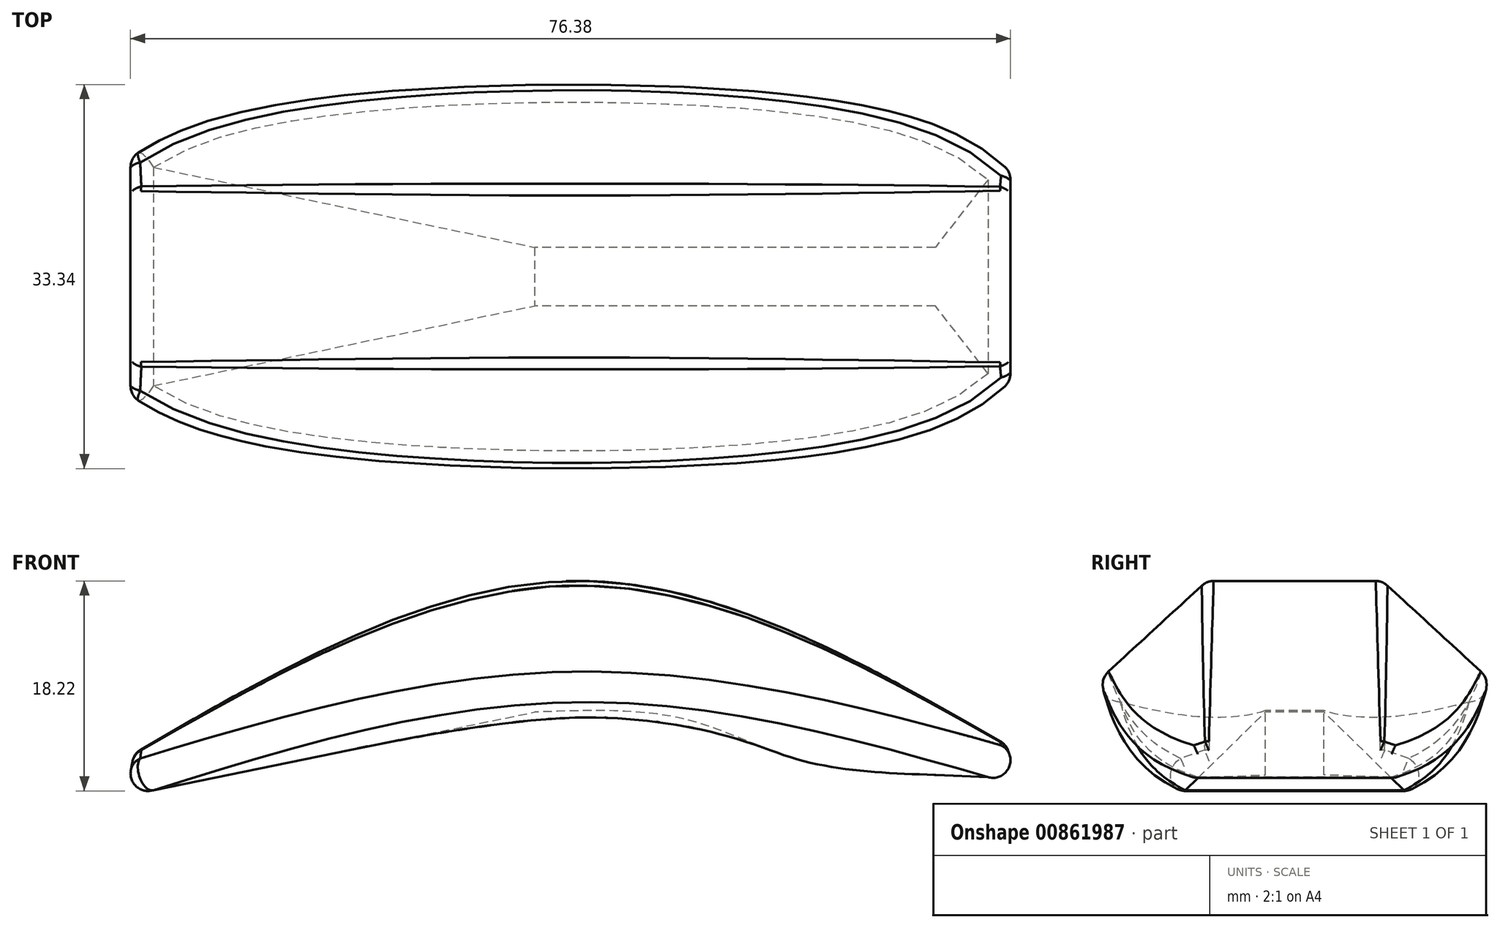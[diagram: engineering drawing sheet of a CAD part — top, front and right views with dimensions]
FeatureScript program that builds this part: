
annotation { "Feature Type Name" : "Feature", "Feature Type Description" : "" }
export const myFeature = defineFeature(function(context is Context, id is Id, definition is map)
    precondition{}
    {
        {
            var Q0;
            Q0=qCreatedBy(makeId("Front.planeOp"),FACE);
            var sketch = newSketch(context, id + "F0", { "sketchPlane" : qUnion([Q0])});
            skFitSpline(sketch, "E0", {"points": [v(-39.15, -14.45) * mm, v(0, -6.04) * mm, v(38.63, -13.4) * mm], "startDerivative": vector(78.03, 24.66) * mm, "endDerivative": vector(77.52, -22.63) * mm});
            skSolve(sketch);
        }
        {
            var Q0;
            Q0 = qSketchRegion(id + "F0", true);
            var Q1;
            Q1=sQuery(id+"F0.wireOp",EDGE,"E0");
            extrude(context, id + "F1", {"entities" : qUnion([Q0]), "bodyType" : ToolBodyType.SURFACE, "surfaceEntities" : qUnion([Q1]), "endBound" : BoundingType.SYMMETRIC, "depth" : 38.1 * mm, "offsetDistance" : 25.4 * mm});
        }
        {
            var Q0;
            Q0=qCreatedBy(makeId("Front.planeOp"),FACE);
            var sketch = newSketch(context, id + "F2", { "sketchPlane" : qUnion([Q0])});
            skFitSpline(sketch, "E1", {"points": [v(-38.4, -10.51) * mm, v(0, 4.47) * mm, v(37.28, -9.72) * mm], "startDerivative": vector(76.42, 44.41) * mm, "endDerivative": vector(74.92, -43.07) * mm});
            skSolve(sketch);
        }
        {
            var Q0;
            Q0 = qSketchRegion(id + "F2", true);
            var Q1;
            Q1=sQuery(id+"F2.wireOp",EDGE,"E1");
            extrude(context, id + "F3", {"entities" : qUnion([Q0]), "bodyType" : ToolBodyType.SURFACE, "surfaceEntities" : qUnion([Q1]), "endBound" : BoundingType.SYMMETRIC, "depth" : 15.24 * mm, "offsetDistance" : 25.4 * mm});
        }
        {
            var Q0;
            Q0=makeQuery(id+"F3.opExtrude","SWEPT_FACE",FACE,{"disambiguationData":[OSD([sQuery(id+"F2.wireOp",EDGE,"E1")])]});
            var Q1;
            Q1=makeQuery(id+"F1.opExtrude","SWEPT_FACE",FACE,{"disambiguationData":[OSD([sQuery(id+"F0.wireOp",EDGE,"E0")])]});
            loft(context, id + "F4", {"sheetProfilesArray" : [{ "sheetProfileEntities" : qUnion([Q0]) }, { "sheetProfileEntities" : qUnion([Q1]) }]});
        }
        {
            var Q0;
            Q0=makeQuery(id+"F4.opLoft","SWEPT_FACE",FACE,{"disambiguationData":[OSD([sQuery(id+"F0.wireOp",VERTEX,"E0.start"),sQuery(id+"F2.wireOp",VERTEX,"E1.start")])]});
            var Q1;
            {var subQ0=sQuery(id+"F2.wireOp",EDGE,"E1");var subQ1=sQuery(id+"F2.wireOp",VERTEX,"E1.end");var subQ2=sQuery(id+"F2.wireOp",VERTEX,"E1.start");var subQ3=sQuery(id+"F0.wireOp",EDGE,"E0");var subQ4=sQuery(id+"F0.wireOp",VERTEX,"E0.end");var subQ5=sQuery(id+"F0.wireOp",VERTEX,"E0.start");Q1=makeQuery(id+"F4.opLoft","SWEPT_FACE",FACE,{"disambiguationData":[OSD([subQ5,subQ4,subQ3,subQ2,subQ1,subQ0]),TDD([makeQuery(id+"F1.opExtrude","CAP_VERTEX",VERTEX,{"disambiguationData":[OSD([subQ5])],"isStart":false}),makeQuery(id+"F1.opExtrude","CAP_VERTEX",VERTEX,{"disambiguationData":[OSD([subQ4])],"isStart":false}),makeQuery(id+"F1.opExtrude","CAP_EDGE",EDGE,{"disambiguationData":[OSD([subQ3])],"isStart":false}),makeQuery(id+"F3.opExtrude","CAP_VERTEX",VERTEX,{"disambiguationData":[OSD([subQ2])],"isStart":false}),makeQuery(id+"F3.opExtrude","CAP_VERTEX",VERTEX,{"disambiguationData":[OSD([subQ1])],"isStart":false}),makeQuery(id+"F3.opExtrude","CAP_EDGE",EDGE,{"disambiguationData":[OSD([subQ0])],"isStart":false})])]});}
            var Q2;
            Q2=makeQuery(id+"F4.opLoft","SWEPT_FACE",FACE,{"disambiguationData":[OSD([sQuery(id+"F0.wireOp",VERTEX,"E0.end"),sQuery(id+"F2.wireOp",VERTEX,"E1.end")])]});
            var Q3;
            {var subQ0=sQuery(id+"F2.wireOp",EDGE,"E1");var subQ1=sQuery(id+"F2.wireOp",VERTEX,"E1.end");var subQ2=sQuery(id+"F2.wireOp",VERTEX,"E1.start");var subQ3=sQuery(id+"F0.wireOp",EDGE,"E0");var subQ4=sQuery(id+"F0.wireOp",VERTEX,"E0.end");var subQ5=sQuery(id+"F0.wireOp",VERTEX,"E0.start");Q3=makeQuery(id+"F4.opLoft","SWEPT_FACE",FACE,{"disambiguationData":[OSD([subQ5,subQ4,subQ3,subQ2,subQ1,subQ0]),TDD([makeQuery(id+"F1.opExtrude","CAP_VERTEX",VERTEX,{"disambiguationData":[OSD([subQ5])],"isStart":true}),makeQuery(id+"F1.opExtrude","CAP_VERTEX",VERTEX,{"disambiguationData":[OSD([subQ4])],"isStart":true}),makeQuery(id+"F1.opExtrude","CAP_EDGE",EDGE,{"disambiguationData":[OSD([subQ3])],"isStart":true}),makeQuery(id+"F3.opExtrude","CAP_VERTEX",VERTEX,{"disambiguationData":[OSD([subQ2])],"isStart":true}),makeQuery(id+"F3.opExtrude","CAP_VERTEX",VERTEX,{"disambiguationData":[OSD([subQ1])],"isStart":true}),makeQuery(id+"F3.opExtrude","CAP_EDGE",EDGE,{"disambiguationData":[OSD([subQ0])],"isStart":true})])]});}
            fillet(context, id + "F5", {"entities" : qUnion([Q0, Q1, Q2, Q3]), "radius" : 1.52 * mm, "tangentPropagation" : true, "allowEdgeOverflow" : false});
        }
        {
            var Q0;
            Q0=qCreatedBy(makeId("Front.planeOp"),FACE);
            var sketch = newSketch(context, id + "F6", { "sketchPlane" : qUnion([Q0])});
            skFitSpline(sketch, "E2", {"points": [v(31.15, -12.37) * mm, v(19.3, -11.04) * mm, v(9.34, -7.5) * mm, v(-3.63, -6.91) * mm], "startDerivative": vector(-36.8, 1.35) * mm, "endDerivative": vector(-38.9, -1.46) * mm});
            skSolve(sketch);
        }
        {
            var Q0;
            Q0=sQuery(id+"F6.wireOp",EDGE,"E2");
            extrude(context, id + "F7", {"bodyType" : ToolBodyType.SURFACE, "surfaceEntities" : qUnion([Q0]), "endBound" : BoundingType.SYMMETRIC, "depth" : 5.08 * mm, "offsetDistance" : 25.4 * mm});
        }
        {
            var Q1;
            Q1=makeQuery(id+"F4.opLoft","CAP_FACE",FACE,{"disambiguationData":[OSD([sQuery(id+"F0.wireOp",EDGE,"E0")])],"isStart":true});
            var Q2;
            Q2=makeQuery(id+"F7.opExtrude","SWEPT_FACE",FACE,{"disambiguationData":[OSD([sQuery(id+"F6.wireOp",EDGE,"E2")])]});
            loft(context, id + "F8", {"operationType" : NewBodyOperationType.ADD, "sheetProfilesArray" : [{ "sheetProfileEntities" : qUnion([Q1]) }, { "sheetProfileEntities" : qUnion([Q2]) }]});
        }
    });
